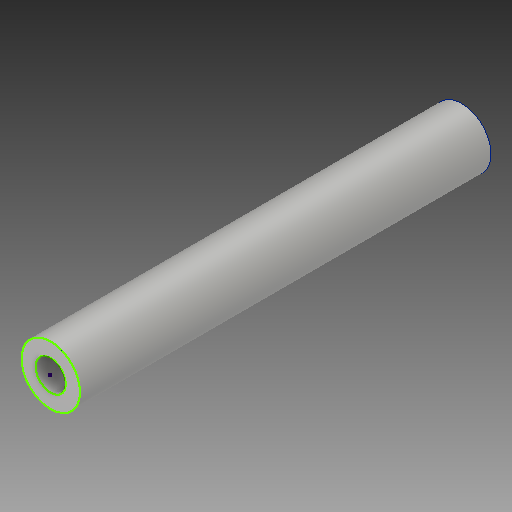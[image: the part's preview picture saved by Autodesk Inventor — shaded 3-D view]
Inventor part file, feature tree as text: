
AUTODESK INVENTOR PART (.ipt)
format: ipt  version: 2017 (Build 210142000, 142)  size: 93,696 bytes
history: native  units: in
note: dims shown in document units (in); Inventor stores cm internally (conversion verified against a paired STEP export)
features: sketch x2, extrude x1
ambient origin geometry x8: Origin, YZ Plane, XZ Plane, XY Plane, X Axis, Y Axis, Z Axis, Center Point
bodies: Solid1 (feature_tree)
feature tree (3):
  extrude  "Extrusion1"  [1 undecoded]
  sketch  "Sketch3"
  sketch  "Sketch1"  dims[d0=3.5in d1=0.0in]
note: 1 required parameter value undecoded (feature->parameter linkage not recoverable at this tier; creation-order binding heuristic only, values carry confidence <= 0.55)
